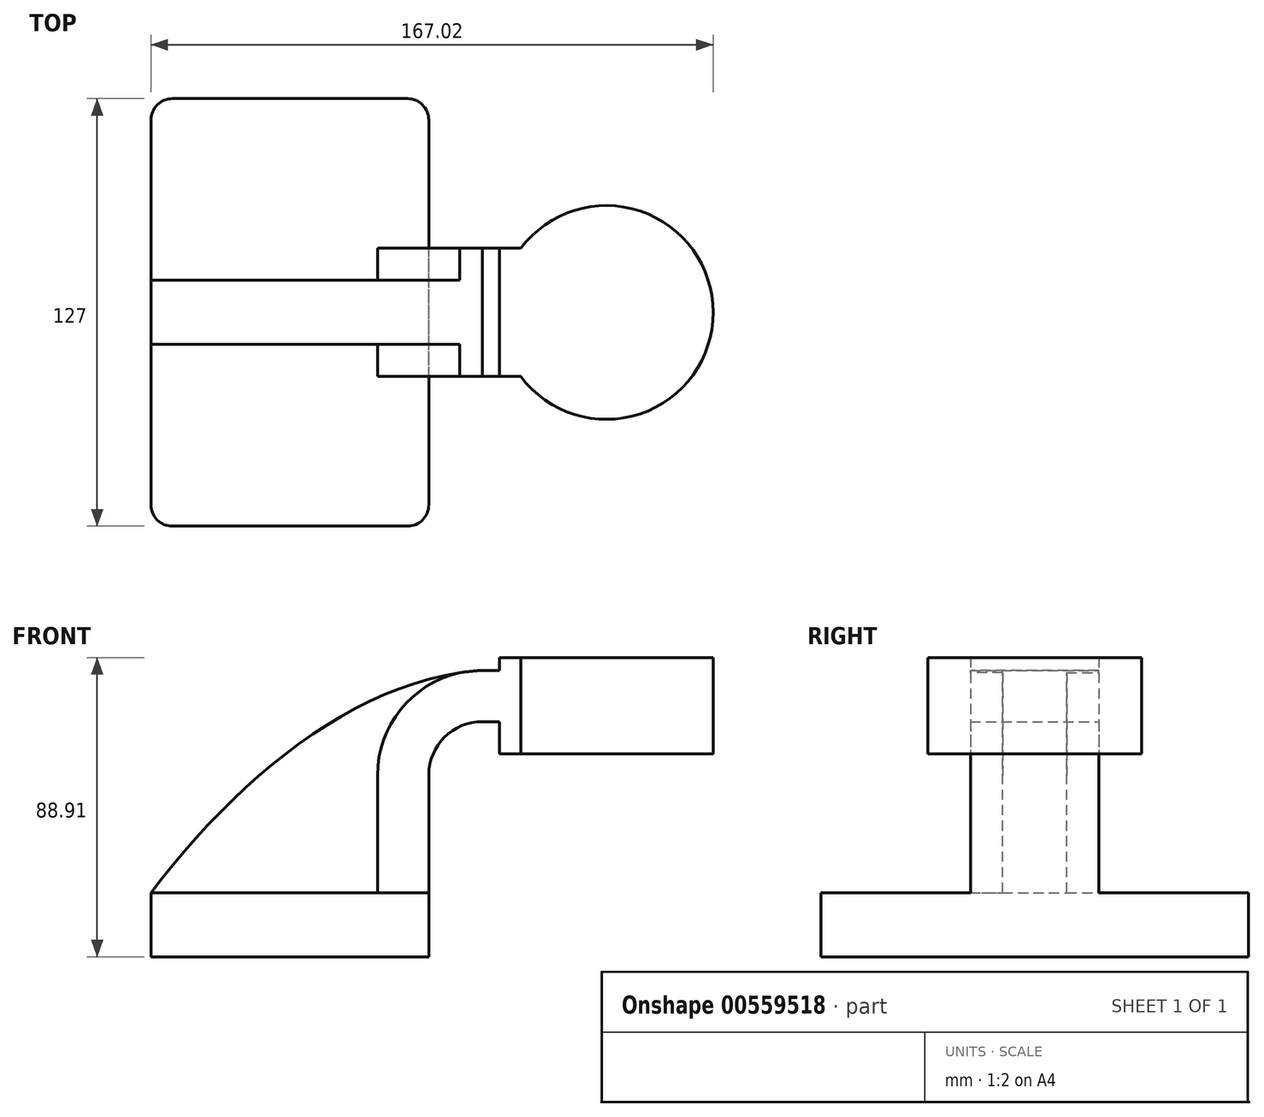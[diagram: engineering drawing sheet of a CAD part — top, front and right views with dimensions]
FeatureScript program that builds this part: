
annotation { "Feature Type Name" : "Feature", "Feature Type Description" : "" }
export const myFeature = defineFeature(function(context is Context, id is Id, definition is map)
    precondition{}
    {
        {
            var Q0;
            Q0=qCreatedBy(makeId("Front.planeOp"),FACE);
            var sketch = newSketch(context, id + "F0", { "sketchPlane" : qUnion([Q0])});
            skLineSegment(sketch, "E0.bottom", {"start": v(-41.28, 9.52) * mm, "end": v(41.27, 9.53) * mm});
            skLineSegment(sketch, "E0.top", {"start": v(-41.28, -9.52) * mm, "end": v(41.28, -9.52) * mm});
            skLineSegment(sketch, "E0.left", {"start": v(-41.28, 9.52) * mm, "end": v(-41.28, -9.53) * mm});
            skLineSegment(sketch, "E0.right", {"start": v(41.27, 9.53) * mm, "end": v(41.28, -9.52) * mm});
            skPoint(sketch, "E0.middle", {"position": v(0, 0) * mm});
            skLineSegment(sketch, "E1.bottom", {"start": v(62.24, 79.38) * mm, "end": v(125.74, 79.38) * mm});
            skLineSegment(sketch, "E1.top", {"start": v(62.24, 50.8) * mm, "end": v(125.74, 50.8) * mm});
            skLineSegment(sketch, "E1.left", {"start": v(62.24, 79.38) * mm, "end": v(62.24, 50.8) * mm});
            skLineSegment(sketch, "E1.right", {"start": v(125.74, 79.38) * mm, "end": v(125.74, 50.8) * mm});
            skPoint(sketch, "E1.middle", {"position": v(94, 65.09) * mm});
            skLineSegment(sketch, "E2", {"start": v(41.27, 9.53) * mm, "end": v(41.27, 44.45) * mm});
            skArc(sketch, "E3", {"start": v(41.27, 44.45) * mm, "mid": v(45.92, 55.68) * mm, "end": v(57.15, 60.33) * mm});
            skLineSegment(sketch, "E4", {"start": v(57.15, 60.33) * mm, "end": v(93.95, 60.33) * mm});
            skLineSegment(sketch, "E5.0", {"start": v(57.15, 75.57) * mm, "end": v(93.95, 75.57) * mm});
            skArc(sketch, "E5.1", {"start": v(26.03, 44.45) * mm, "mid": v(35.15, 66.45) * mm, "end": v(57.15, 75.57) * mm});
            skLineSegment(sketch, "E5.2", {"start": v(26.03, 9.53) * mm, "end": v(26.03, 44.45) * mm});
            skLineSegment(sketch, "E6", {"start": v(94, 50.8) * mm, "end": v(94, 79.38) * mm});
            skFitSpline(sketch, "E7", {"points": [v(-41.28, 9.52) * mm, v(57.15, 75.57) * mm], "startDerivative": vector(77.68, 102.06) * mm, "endDerivative": vector(112.42, 7.45) * mm});
            skSolve(sketch);
        }
        {
            var Q0;
            Q0=makeQuery(id+"F0.imprint","IMPRINT",FACE,{"disambiguationData":[TD([[makeQuery(id+"F0.imprint","IMPRINT",EDGE,{"derivedFrom":sQuery(id+"F0.wireOp",EDGE,"E0.top")}),1.0]])]});
            extrude(context, id + "F1", {"entities" : qUnion([Q0]), "endBound" : BoundingType.SYMMETRIC, "depth" : 127 * mm, "offsetDistance" : 25.4 * mm});
        }
        {
            var Q0;
            {var subQ3=sQuery(id+"F0.wireOp",EDGE,"E5.2");Q0=makeQuery(id+"F0.imprint","IMPRINT",FACE,{"disambiguationData":[TD([[makeQuery(id+"F0.imprint","IMPRINT",EDGE,{"derivedFrom":subQ3}),1.0]])]});}
            extrude(context, id + "F2", {"entities" : qUnion([Q0]), "operationType" : NewBodyOperationType.ADD, "endBound" : BoundingType.SYMMETRIC, "depth" : 19.05 * mm, "offsetDistance" : 25.4 * mm});
        }
        {
            var Q0;
            {var subQ1=sQuery(id+"F0.wireOp",EDGE,"E2");Q0=makeQuery(id+"F0.imprint","IMPRINT",FACE,{"disambiguationData":[TD([[makeQuery(id+"F0.imprint","IMPRINT",EDGE,{"derivedFrom":subQ1}),1.0]])]});}
            var Q1;
            {var subQ4=sQuery(id+"F0.wireOp",EDGE,"E6");Q1=makeQuery(id+"F0.imprint","IMPRINT",FACE,{"disambiguationData":[TD([[makeQuery(id+"F0.imprint","IMPRINT",EDGE,{"derivedFrom":subQ4}),1.0]])]});}
            extrude(context, id + "F3", {"entities" : qUnion([Q0, Q1]), "operationType" : NewBodyOperationType.ADD, "endBound" : BoundingType.SYMMETRIC, "depth" : 38.1 * mm, "offsetDistance" : 25.4 * mm});
        }
        {
            var Q0;
            {var subQ0=sQuery(id+"F0.wireOp",EDGE,"E1.right");Q0=makeQuery(id+"F0.imprint","IMPRINT",FACE,{"disambiguationData":[TD([[makeQuery(id+"F0.imprint","IMPRINT",EDGE,{"derivedFrom":subQ0}),-1.0]])]});}
            var Q1;
            Q1=sQuery(id+"F0.wireOp",EDGE,"E6");
            revolve(context, id + "F4", {"operationType" : NewBodyOperationType.ADD, "entities" : qUnion([Q0]), "axis" : qUnion([Q1]), "revolveType" : RevolveType.FULL});
        }
        {
            var Q0;
            Q0=makeQuery(id+"F1.opExtrude","CAP_EDGE",EDGE,{"disambiguationData":[OSD([sQuery(id+"F0.wireOp",EDGE,"E0.right")])],"isStart":true});
            var Q1;
            Q1=makeQuery(id+"F1.opExtrude","CAP_EDGE",EDGE,{"disambiguationData":[OSD([sQuery(id+"F0.wireOp",EDGE,"E0.left")])],"isStart":true});
            var Q2;
            Q2=makeQuery(id+"F1.opExtrude","CAP_EDGE",EDGE,{"disambiguationData":[OSD([sQuery(id+"F0.wireOp",EDGE,"E0.right")])],"isStart":false});
            var Q3;
            Q3=makeQuery(id+"F1.opExtrude","CAP_EDGE",EDGE,{"disambiguationData":[OSD([sQuery(id+"F0.wireOp",EDGE,"E0.left")])],"isStart":false});
            fillet(context, id + "F5", {"entities" : qUnion([Q0, Q1, Q2, Q3]), "radius" : 6.35 * mm, "tangentPropagation" : true, "allowEdgeOverflow" : false});
        }
    });
